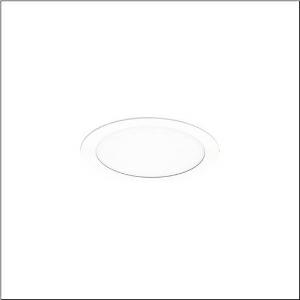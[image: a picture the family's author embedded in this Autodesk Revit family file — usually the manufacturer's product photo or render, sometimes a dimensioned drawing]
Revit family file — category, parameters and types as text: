
# Revit family: lunis_21_l_51db16md91c
name_source: partatom
category: Lighting Fixtures
units: mm (PartAtom-declared; Revit-internal decimal feet)

## family parameters
Cut with Voids When Loaded = No
Host = Face
Light Source = No
Part Type = Normal
Room Calculation Point = No
Round Connector Dimension = Use Diameter
Shared = No

## types (1)
- --- (1 x LED, 3020 lm, 21.7 W, 6500K)
    Apparent Load = 22 VA
    CIE Flux Codes = 50 80 96 100 100
    Color Rendering = 80
    Color Temperature = 6500K
    Default Elevation = 1800 mm
    Description = Lunis 21,  L, downlight, light control with lens, of PMMA, optical cover: cover panel, of PC, opal, light emission: direct distribution, LED rated luminous flux: 1.750lm, light colour: 830/840/865, with terminal, 3-pole, mains connection: 220..240V, AC/DC, 0/50..60Hz, housing, round, of diecast aluminium, traffic white (RAL 9016), diameter: 165mm, clamping range: 1..40mm, protection rating (complete): IP20, protection rating (on room side): IP54, insulation class (complete): insulation class II (safety insulation), certification: CE, impact resistance: IK03, packaging unit: 1 piece
    Height = 0 mm  [stored 0 ft]
    Lamp = 1 x LED
    Lamp Light Flux = 3020 lm
    Lamp Power = 21.7 W
    Lamp count = 1
    Length = 165 mm
    Luminous efficacy = 139 lm/W
    Manufacturer = Siteco
    ModVariant = No
    Model = 51DB16MD91C
    Mounting Place = Ceiling
    Mounting Type = Recessed
    Number of Poles = 1
    OnlyDefault = Yes
    Power Factor = 1
    Product Name = Lunis 21 L
    Product group = downlight
    ProductGroupID = 401
    Protection Class = Protection class II
    Protection Degree = IP 20
    RLX_Detail_Level = 1
    RLX_Emergency_Light_Flux = 0 lm
    RLX_Emergency_Type = 0
    RLX_Emergency_Type_DB = No
    RlxData = <blob elided: 13721 chars, md5=b10aa52c>
    Socket = socket
    Standby Power = 0 W
    System Light Flux = 3020 lm
    System Power = 22 W
    Type Comments = individual setting: colour temperature 6500K, luminous flux: 100 % | (OFF | ON | ON | ON) | 650 mA
    Type Image = l_1291165.jpg
    URL = http://relux.com
    VarID = @adj_041011
    Voltage = 0 V
    Weight = 0.00 kg
    Width = 0 mm  [stored 0 ft]

note: [stored X ft] marks values corroborated as IEEE doubles in the binary element streams (Revit-internal decimal feet)

## geometry (parser evidence)
native form markers: Sweep x11
no freeform markers — native parametric forms only
